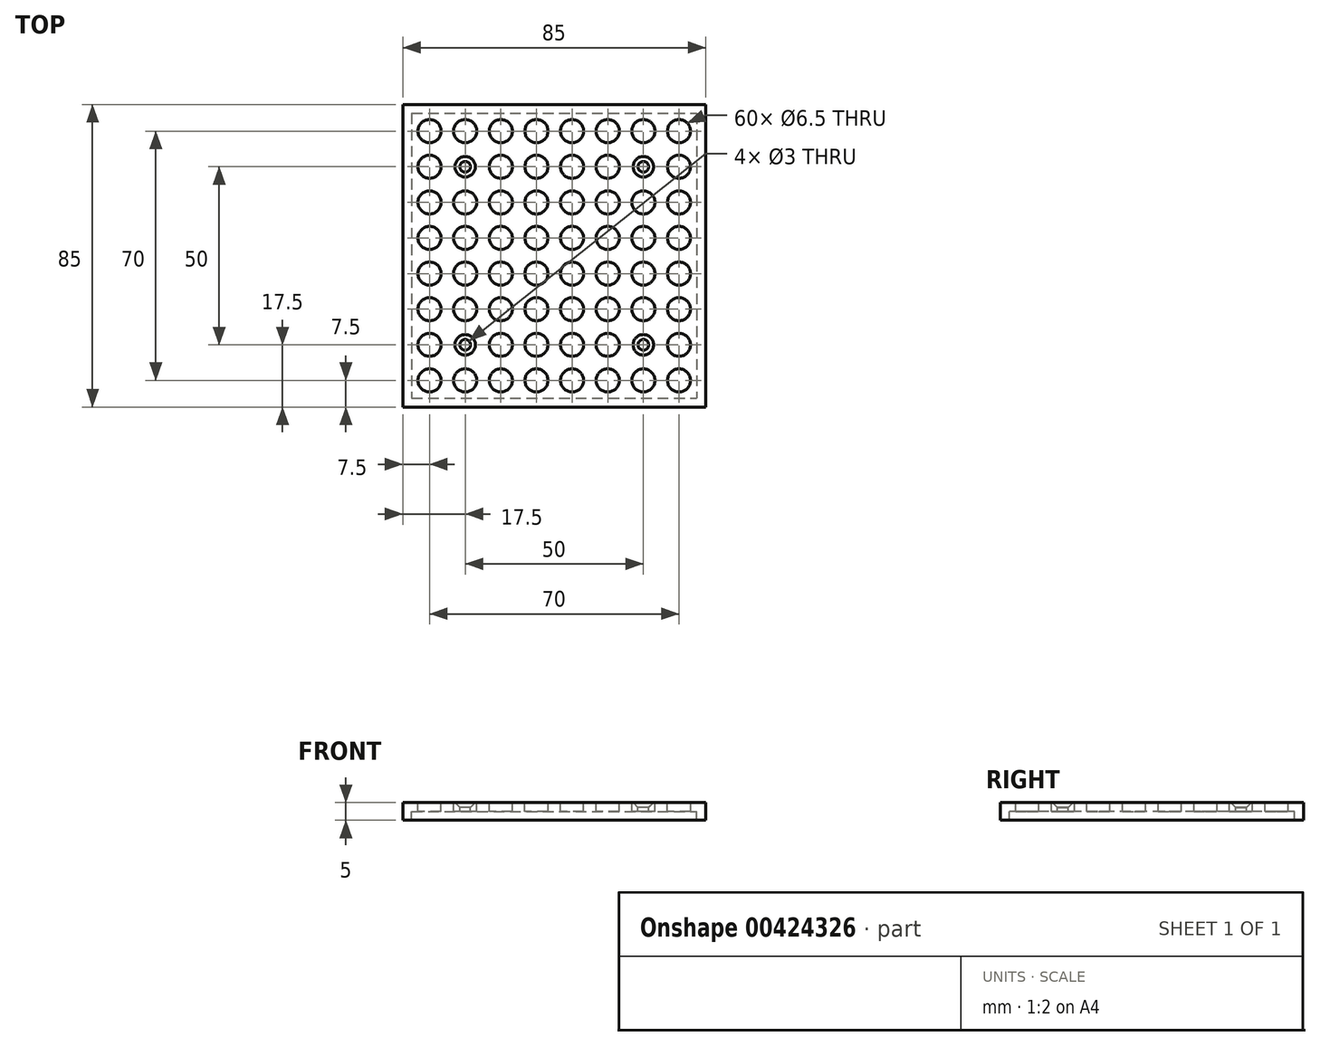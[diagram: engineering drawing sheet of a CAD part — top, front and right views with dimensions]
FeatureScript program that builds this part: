
annotation { "Feature Type Name" : "Feature", "Feature Type Description" : "" }
export const myFeature = defineFeature(function(context is Context, id is Id, definition is map)
    precondition{}
    {
        {
            var Q0;
            Q0=qCreatedBy(makeId("Top.planeOp"),FACE);
            var sketch = newSketch(context, id + "F0", { "sketchPlane" : qUnion([Q0])});
            skLineSegment(sketch, "E0.bottom", {"start": v(42.5, 42.5) * mm, "end": v(-42.5, 42.5) * mm});
            skLineSegment(sketch, "E0.top", {"start": v(42.5, -42.5) * mm, "end": v(-42.5, -42.5) * mm});
            skLineSegment(sketch, "E0.left", {"start": v(42.5, 42.5) * mm, "end": v(42.5, -42.5) * mm});
            skLineSegment(sketch, "E0.right", {"start": v(-42.5, 42.5) * mm, "end": v(-42.5, -42.5) * mm});
            skPoint(sketch, "E0.middle", {"position": v(0, 0) * mm});
            skCircle(sketch, "E1", {"center": v(-35, 35) * mm, "radius": 3.25 * mm});
            skCircle(sketch, "E2.0.1.0", {"center": v(-35, 25) * mm, "radius": 3.25 * mm});
            skCircle(sketch, "E2.0.2.0", {"center": v(-35, 15) * mm, "radius": 3.25 * mm});
            skCircle(sketch, "E2.0.3.0", {"center": v(-35, 5) * mm, "radius": 3.25 * mm});
            skCircle(sketch, "E2.0.4.0", {"center": v(-35, -5) * mm, "radius": 3.25 * mm});
            skCircle(sketch, "E2.0.5.0", {"center": v(-35, -15) * mm, "radius": 3.25 * mm});
            skCircle(sketch, "E2.0.6.0", {"center": v(-35, -25) * mm, "radius": 3.25 * mm});
            skCircle(sketch, "E2.0.7.0", {"center": v(-35, -35) * mm, "radius": 3.25 * mm});
            skCircle(sketch, "E2.1.0.0", {"center": v(-25, 35) * mm, "radius": 3.25 * mm});
            skCircle(sketch, "E2.1.2.0", {"center": v(-25, 15) * mm, "radius": 3.25 * mm});
            skCircle(sketch, "E2.1.3.0", {"center": v(-25, 5) * mm, "radius": 3.25 * mm});
            skCircle(sketch, "E2.1.4.0", {"center": v(-25, -5) * mm, "radius": 3.25 * mm});
            skCircle(sketch, "E2.1.5.0", {"center": v(-25, -15) * mm, "radius": 3.25 * mm});
            skCircle(sketch, "E2.1.7.0", {"center": v(-25, -35) * mm, "radius": 3.25 * mm});
            skCircle(sketch, "E2.2.0.0", {"center": v(-15, 35) * mm, "radius": 3.25 * mm});
            skCircle(sketch, "E2.2.1.0", {"center": v(-15, 25) * mm, "radius": 3.25 * mm});
            skCircle(sketch, "E2.2.2.0", {"center": v(-15, 15) * mm, "radius": 3.25 * mm});
            skCircle(sketch, "E2.2.3.0", {"center": v(-15, 5) * mm, "radius": 3.25 * mm});
            skCircle(sketch, "E2.2.4.0", {"center": v(-15, -5) * mm, "radius": 3.25 * mm});
            skCircle(sketch, "E2.2.5.0", {"center": v(-15, -15) * mm, "radius": 3.25 * mm});
            skCircle(sketch, "E2.2.6.0", {"center": v(-15, -25) * mm, "radius": 3.25 * mm});
            skCircle(sketch, "E2.2.7.0", {"center": v(-15, -35) * mm, "radius": 3.25 * mm});
            skCircle(sketch, "E2.3.0.0", {"center": v(-5, 35) * mm, "radius": 3.25 * mm});
            skCircle(sketch, "E2.3.1.0", {"center": v(-5, 25) * mm, "radius": 3.25 * mm});
            skCircle(sketch, "E2.3.2.0", {"center": v(-5, 15) * mm, "radius": 3.25 * mm});
            skCircle(sketch, "E2.3.3.0", {"center": v(-5, 5) * mm, "radius": 3.25 * mm});
            skCircle(sketch, "E2.3.4.0", {"center": v(-5, -5) * mm, "radius": 3.25 * mm});
            skCircle(sketch, "E2.3.5.0", {"center": v(-5, -15) * mm, "radius": 3.25 * mm});
            skCircle(sketch, "E2.3.6.0", {"center": v(-5, -25) * mm, "radius": 3.25 * mm});
            skCircle(sketch, "E2.3.7.0", {"center": v(-5, -35) * mm, "radius": 3.25 * mm});
            skCircle(sketch, "E2.4.0.0", {"center": v(5, 35) * mm, "radius": 3.25 * mm});
            skCircle(sketch, "E2.4.1.0", {"center": v(5, 25) * mm, "radius": 3.25 * mm});
            skCircle(sketch, "E2.4.2.0", {"center": v(5, 15) * mm, "radius": 3.25 * mm});
            skCircle(sketch, "E2.4.3.0", {"center": v(5, 5) * mm, "radius": 3.25 * mm});
            skCircle(sketch, "E2.4.4.0", {"center": v(5, -5) * mm, "radius": 3.25 * mm});
            skCircle(sketch, "E2.4.5.0", {"center": v(5, -15) * mm, "radius": 3.25 * mm});
            skCircle(sketch, "E2.4.6.0", {"center": v(5, -25) * mm, "radius": 3.25 * mm});
            skCircle(sketch, "E2.4.7.0", {"center": v(5, -35) * mm, "radius": 3.25 * mm});
            skCircle(sketch, "E2.5.0.0", {"center": v(15, 35) * mm, "radius": 3.25 * mm});
            skCircle(sketch, "E2.5.1.0", {"center": v(15, 25) * mm, "radius": 3.25 * mm});
            skCircle(sketch, "E2.5.2.0", {"center": v(15, 15) * mm, "radius": 3.25 * mm});
            skCircle(sketch, "E2.5.3.0", {"center": v(15, 5) * mm, "radius": 3.25 * mm});
            skCircle(sketch, "E2.5.4.0", {"center": v(15, -5) * mm, "radius": 3.25 * mm});
            skCircle(sketch, "E2.5.5.0", {"center": v(15, -15) * mm, "radius": 3.25 * mm});
            skCircle(sketch, "E2.5.6.0", {"center": v(15, -25) * mm, "radius": 3.25 * mm});
            skCircle(sketch, "E2.5.7.0", {"center": v(15, -35) * mm, "radius": 3.25 * mm});
            skCircle(sketch, "E2.6.0.0", {"center": v(25, 35) * mm, "radius": 3.25 * mm});
            skCircle(sketch, "E2.6.2.0", {"center": v(25, 15) * mm, "radius": 3.25 * mm});
            skCircle(sketch, "E2.6.3.0", {"center": v(25, 5) * mm, "radius": 3.25 * mm});
            skCircle(sketch, "E2.6.4.0", {"center": v(25, -5) * mm, "radius": 3.25 * mm});
            skCircle(sketch, "E2.6.5.0", {"center": v(25, -15) * mm, "radius": 3.25 * mm});
            skCircle(sketch, "E2.6.7.0", {"center": v(25, -35) * mm, "radius": 3.25 * mm});
            skCircle(sketch, "E2.7.0.0", {"center": v(35, 35) * mm, "radius": 3.25 * mm});
            skCircle(sketch, "E2.7.1.0", {"center": v(35, 25) * mm, "radius": 3.25 * mm});
            skCircle(sketch, "E2.7.2.0", {"center": v(35, 15) * mm, "radius": 3.25 * mm});
            skCircle(sketch, "E2.7.3.0", {"center": v(35, 5) * mm, "radius": 3.25 * mm});
            skCircle(sketch, "E2.7.4.0", {"center": v(35, -5) * mm, "radius": 3.25 * mm});
            skCircle(sketch, "E2.7.5.0", {"center": v(35, -15) * mm, "radius": 3.25 * mm});
            skCircle(sketch, "E2.7.6.0", {"center": v(35, -25) * mm, "radius": 3.25 * mm});
            skCircle(sketch, "E2.7.7.0", {"center": v(35, -35) * mm, "radius": 3.25 * mm});
            skLineSegment(sketch, "E2.direction1", {"start": v(-35, 35) * mm, "end": v(-25, 35) * mm, "construction": true});
            skLineSegment(sketch, "E2.direction2", {"start": v(-35, 35) * mm, "end": v(-35, 25) * mm, "construction": true});
            skLineSegment(sketch, "E3.bottom", {"start": v(-40, 40) * mm, "end": v(40, 40) * mm});
            skLineSegment(sketch, "E3.top", {"start": v(-40, -40) * mm, "end": v(40, -40) * mm});
            skLineSegment(sketch, "E3.left", {"start": v(-40, 40) * mm, "end": v(-40, -40) * mm});
            skLineSegment(sketch, "E3.right", {"start": v(40, 40) * mm, "end": v(40, -40) * mm});
            skPoint(sketch, "E4", {"position": v(25, 25) * mm});
            skPoint(sketch, "E5", {"position": v(25, -25) * mm});
            skPoint(sketch, "E6", {"position": v(-25, -25) * mm});
            skPoint(sketch, "E7", {"position": v(-25, 25) * mm});
            skSolve(sketch);
        }
        {
            var Q0;
            Q0=makeQuery(id+"F0.imprint","IMPRINT",FACE,{"disambiguationData":[TD([[makeQuery(id+"F0.imprint","IMPRINT",EDGE,{"derivedFrom":sQuery(id+"F0.wireOp",EDGE,"E0.bottom")}),1.0]])]});
            extrude(context, id + "F1", {"entities" : qUnion([Q0]), "oppositeDirection" : true, "depth" : 5 * mm});
        }
        {
            var Q0;
            Q0=makeQuery(id+"F0.imprint","IMPRINT",FACE,{"disambiguationData":[TD([[makeQuery(id+"F0.imprint","IMPRINT",EDGE,{"derivedFrom":sQuery(id+"F0.wireOp",EDGE,"E1")}),-1.0]])]});
            extrude(context, id + "F2", {"entities" : qUnion([Q0]), "operationType" : NewBodyOperationType.ADD, "oppositeDirection" : true, "depth" : 2.5 * mm});
        }
        {
            var Q0;
            Q0=sQuery(id+"F0.wireOp",VERTEX,"E7");
            var Q1;
            Q1=sQuery(id+"F0.wireOp",VERTEX,"E4");
            var Q2;
            Q2=sQuery(id+"F0.wireOp",VERTEX,"E5");
            var Q3;
            Q3=sQuery(id+"F0.wireOp",VERTEX,"E6");
            var Q4;
            Q4=makeQuery(id+"F1.opExtrude","SWEPT_BODY",BODY,{"disambiguationData":[OSD([sQuery(id+"F0.wireOp",EDGE,"E0.bottom"),sQuery(id+"F0.wireOp",EDGE,"E0.top"),sQuery(id+"F0.wireOp",EDGE,"E0.left"),sQuery(id+"F0.wireOp",EDGE,"E0.right"),sQuery(id+"F0.wireOp",EDGE,"E3.bottom"),sQuery(id+"F0.wireOp",EDGE,"E3.top"),sQuery(id+"F0.wireOp",EDGE,"E3.left"),sQuery(id+"F0.wireOp",EDGE,"E3.right")])]});
            hole(context, id + "F3", {"style" : HoleStyle.C_SINK, "endStyle" : HoleEndStyle.THROUGH, "holeDiameter" : 3 * mm, "cSinkDiameter" : 5.75 * mm, "cSinkAngle" : 90 * degree, "isTappedThrough" : true, "tappedDepth" : 12 * mm, "tapClearance" : 3, "locations" : qUnion([Q0, Q1, Q2, Q3]), "scope" : qUnion([Q4])});
        }
    });
